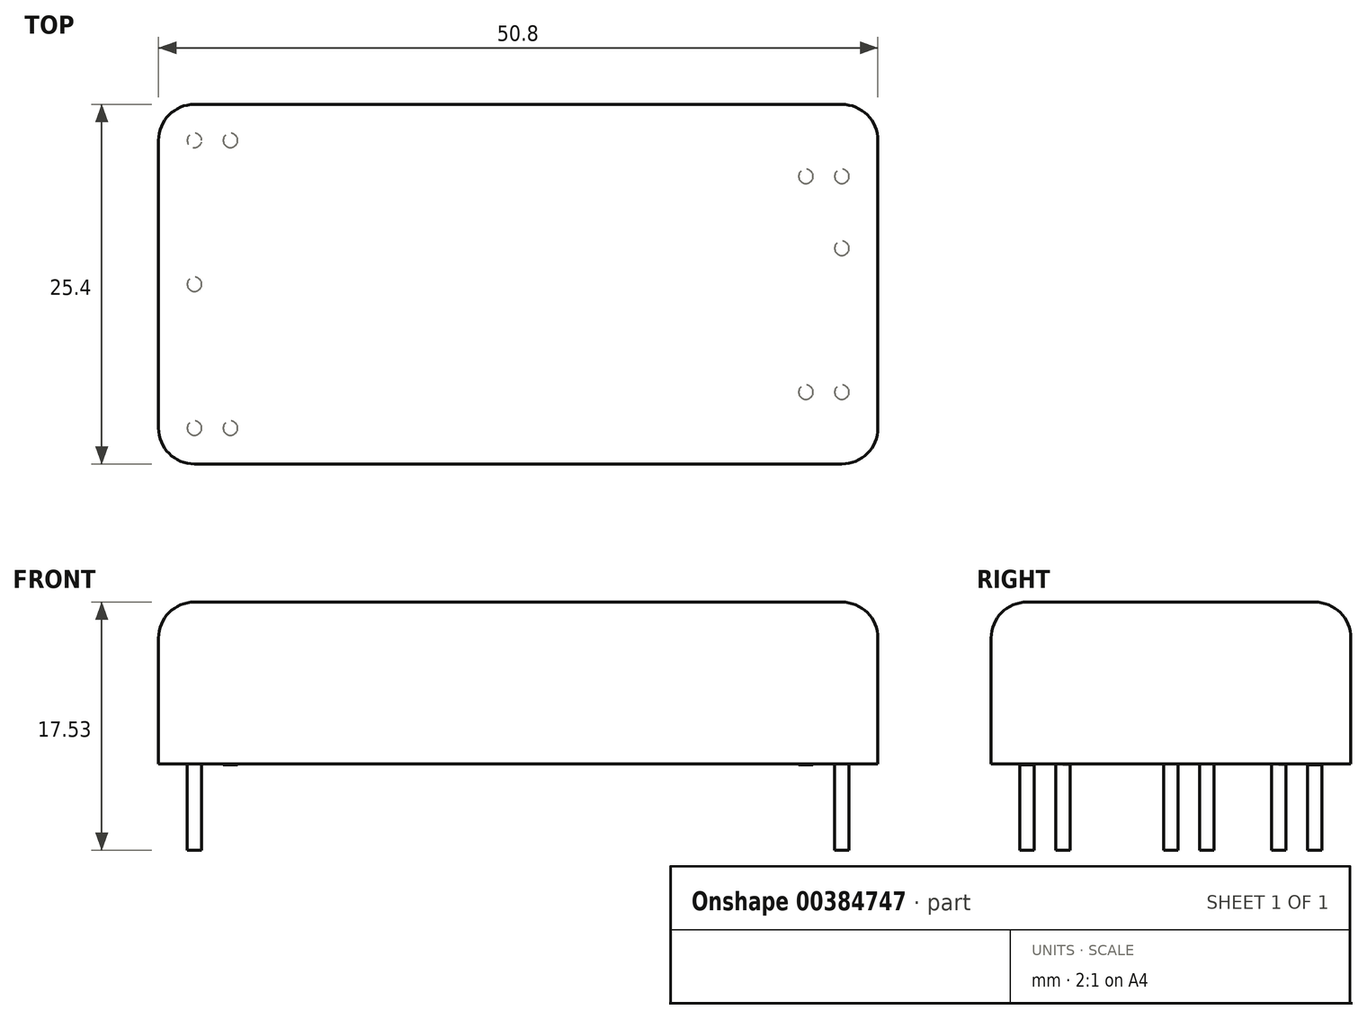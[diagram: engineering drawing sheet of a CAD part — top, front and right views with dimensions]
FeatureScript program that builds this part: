
annotation { "Feature Type Name" : "Feature", "Feature Type Description" : "" }
export const myFeature = defineFeature(function(context is Context, id is Id, definition is map)
    precondition{}
    {
        {
            var Q0;
            Q0=qCreatedBy(makeId("Top.planeOp"),FACE);
            var sketch = newSketch(context, id + "F0", { "sketchPlane" : qUnion([Q0])});
            skLineSegment(sketch, "E0.bottom", {"start": v(25.4, 12.7) * mm, "end": v(-25.4, 12.7) * mm});
            skLineSegment(sketch, "E0.top", {"start": v(25.4, -12.7) * mm, "end": v(-25.4, -12.7) * mm});
            skLineSegment(sketch, "E0.left", {"start": v(25.4, 12.7) * mm, "end": v(25.4, -12.7) * mm});
            skLineSegment(sketch, "E0.right", {"start": v(-25.4, 12.7) * mm, "end": v(-25.4, -12.7) * mm});
            skPoint(sketch, "E0.middle", {"position": v(0, 0) * mm});
            skSolve(sketch);
        }
        {
            var Q0;
            Q0=makeQuery(id+"F0.imprint","IMPRINT",FACE,{"disambiguationData":[TD([[makeQuery(id+"F0.imprint","IMPRINT",EDGE,{"derivedFrom":sQuery(id+"F0.wireOp",EDGE,"E0.bottom")}),1.0]])]});
            extrude(context, id + "F1", {"entities" : qUnion([Q0]), "depth" : 11.43 * mm});
        }
        {
            var Q0;
            Q0=makeQuery(id+"F1.opExtrude","SWEPT_EDGE",EDGE,{"disambiguationData":[OSD([sQuery(id+"F0.wireOp",EDGE,"E0.top"),sQuery(id+"F0.wireOp",EDGE,"E0.left")])]});
            var Q1;
            Q1=makeQuery(id+"F1.opExtrude","SWEPT_EDGE",EDGE,{"disambiguationData":[OSD([sQuery(id+"F0.wireOp",EDGE,"E0.top"),sQuery(id+"F0.wireOp",EDGE,"E0.right")])]});
            var Q2;
            Q2=makeQuery(id+"F1.opExtrude","SWEPT_EDGE",EDGE,{"disambiguationData":[OSD([sQuery(id+"F0.wireOp",EDGE,"E0.bottom"),sQuery(id+"F0.wireOp",EDGE,"E0.left")])]});
            var Q3;
            Q3=makeQuery(id+"F1.opExtrude","SWEPT_EDGE",EDGE,{"disambiguationData":[OSD([sQuery(id+"F0.wireOp",EDGE,"E0.bottom"),sQuery(id+"F0.wireOp",EDGE,"E0.right")])]});
            fillet(context, id + "F2", {"entities" : qUnion([Q0, Q1, Q2, Q3]), "radius" : 2.54 * mm, "tangentPropagation" : true, "allowEdgeOverflow" : false});
        }
        {
            var Q0;
            Q0=makeQuery(id+"F1.opExtrude","CAP_EDGE",EDGE,{"disambiguationData":[OSD([sQuery(id+"F0.wireOp",EDGE,"E0.bottom")])],"isStart":false});
            fillet(context, id + "F3", {"entities" : qUnion([Q0]), "radius" : 2.54 * mm, "tangentPropagation" : true, "allowEdgeOverflow" : false});
        }
        {
            var Q0;
            Q0=makeQuery(id+"F1.opExtrude","CAP_FACE",FACE,{"disambiguationData":[OSD([sQuery(id+"F0.wireOp",EDGE,"E0.bottom"),sQuery(id+"F0.wireOp",EDGE,"E0.top"),sQuery(id+"F0.wireOp",EDGE,"E0.left"),sQuery(id+"F0.wireOp",EDGE,"E0.right")])],"isStart":true});
            var sketch = newSketch(context, id + "F4", { "sketchPlane" : qUnion([Q0])});
            skCircle(sketch, "E1", {"center": v(-22.86, -10.16) * mm, "radius": 0.5 * mm});
            skCircle(sketch, "E2", {"center": v(-22.86, 0) * mm, "radius": 0.5 * mm});
            skCircle(sketch, "E3", {"center": v(-22.86, 10.16) * mm, "radius": 0.5 * mm});
            skCircle(sketch, "E4", {"center": v(22.86, 7.62) * mm, "radius": 0.5 * mm});
            skCircle(sketch, "E5", {"center": v(22.86, -2.54) * mm, "radius": 0.5 * mm});
            skCircle(sketch, "E6", {"center": v(22.86, -7.62) * mm, "radius": 0.5 * mm});
            skCircle(sketch, "E7", {"center": v(-20.32, -10.16) * mm, "radius": 0.5 * mm});
            skCircle(sketch, "E8", {"center": v(-20.32, 10.16) * mm, "radius": 0.5 * mm});
            skCircle(sketch, "E9", {"center": v(20.32, -7.62) * mm, "radius": 0.5 * mm});
            skCircle(sketch, "E10", {"center": v(20.32, 7.62) * mm, "radius": 0.5 * mm});
            skSolve(sketch);
        }
        {
            var Q0;
            Q0=makeQuery(id+"F4.imprint","IMPRINT",FACE,{"disambiguationData":[TD([[makeQuery(id+"F4.imprint","IMPRINT",EDGE,{"derivedFrom":sQuery(id+"F4.wireOp",EDGE,"E4")}),1.0]])]});
            var Q1;
            Q1=makeQuery(id+"F4.imprint","IMPRINT",FACE,{"disambiguationData":[TD([[makeQuery(id+"F4.imprint","IMPRINT",EDGE,{"derivedFrom":sQuery(id+"F4.wireOp",EDGE,"E5")}),1.0]])]});
            var Q2;
            Q2=makeQuery(id+"F4.imprint","IMPRINT",FACE,{"disambiguationData":[TD([[makeQuery(id+"F4.imprint","IMPRINT",EDGE,{"derivedFrom":sQuery(id+"F4.wireOp",EDGE,"E6")}),1.0]])]});
            var Q3;
            Q3=makeQuery(id+"F4.imprint","IMPRINT",FACE,{"disambiguationData":[TD([[makeQuery(id+"F4.imprint","IMPRINT",EDGE,{"derivedFrom":sQuery(id+"F4.wireOp",EDGE,"E1")}),1.0]])]});
            var Q4;
            Q4=makeQuery(id+"F4.imprint","IMPRINT",FACE,{"disambiguationData":[TD([[makeQuery(id+"F4.imprint","IMPRINT",EDGE,{"derivedFrom":sQuery(id+"F4.wireOp",EDGE,"E2")}),1.0]])]});
            var Q5;
            Q5=makeQuery(id+"F4.imprint","IMPRINT",FACE,{"disambiguationData":[TD([[makeQuery(id+"F4.imprint","IMPRINT",EDGE,{"derivedFrom":sQuery(id+"F4.wireOp",EDGE,"E3")}),1.0]])]});
            extrude(context, id + "F5", {"entities" : qUnion([Q0, Q1, Q2, Q3, Q4, Q5]), "operationType" : NewBodyOperationType.ADD, "depth" : 6.1 * mm});
        }
        {
            var Q0;
            Q0 = qSketchRegion(id + "F4", true);
            extrude(context, id + "F6", {"entities" : qUnion([Q0]), "operationType" : NewBodyOperationType.ADD, "depth" : 0.05 * mm});
        }
    });
